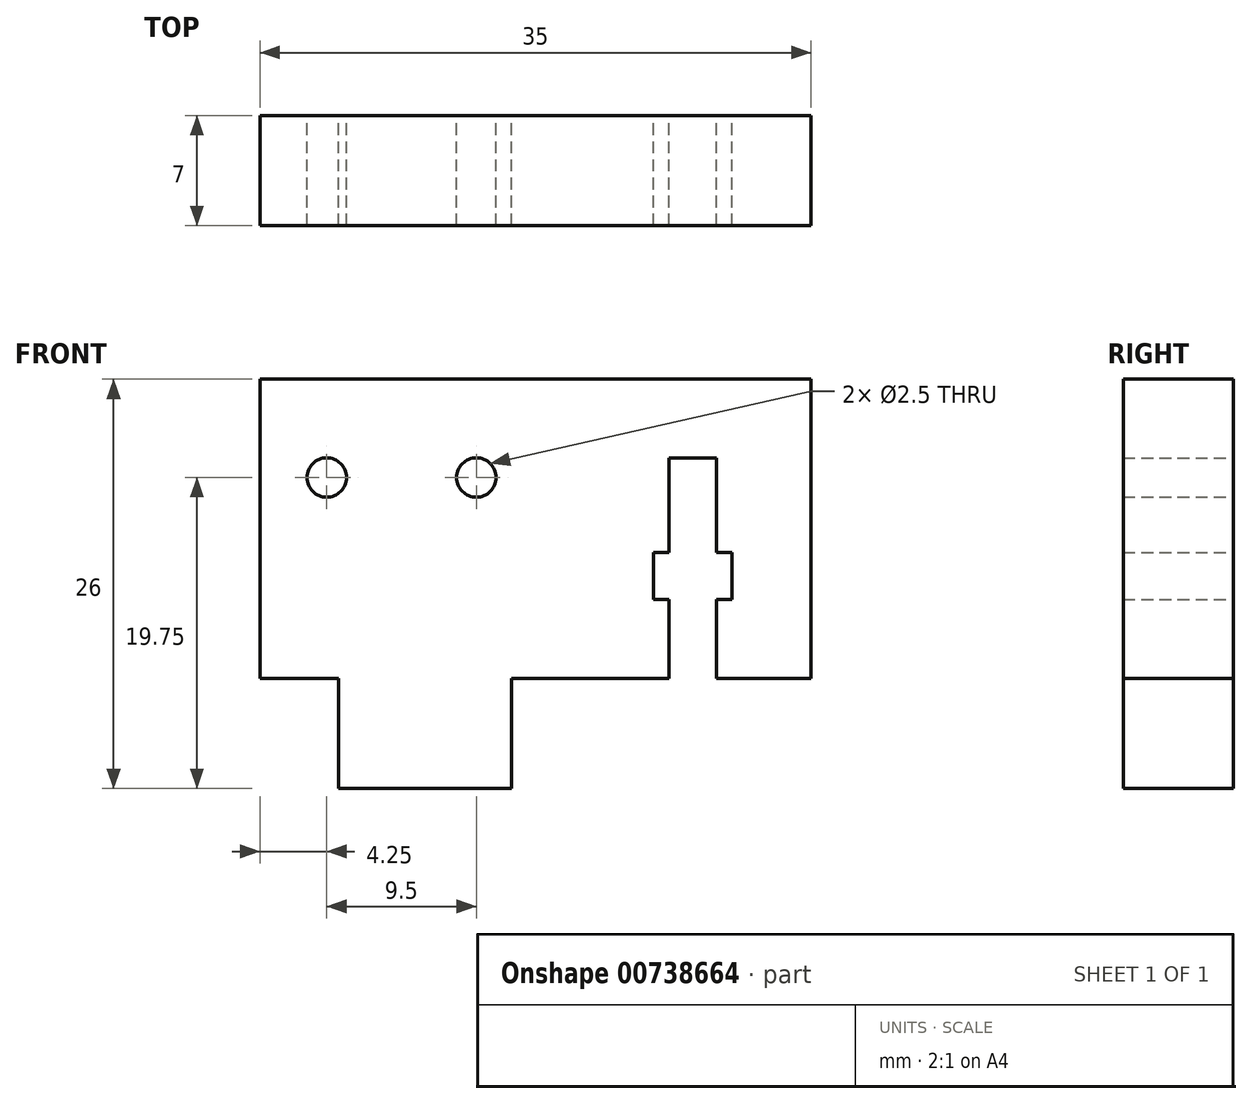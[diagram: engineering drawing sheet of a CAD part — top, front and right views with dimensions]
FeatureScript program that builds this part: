
annotation { "Feature Type Name" : "Feature", "Feature Type Description" : "" }
export const myFeature = defineFeature(function(context is Context, id is Id, definition is map)
    precondition{}
    {
        {
            var Q0;
            Q0=qCreatedBy(makeId("Front.planeOp"),FACE);
            var sketch = newSketch(context, id + "F0", { "sketchPlane" : qUnion([Q0])});
            skLineSegment(sketch, "E0", {"start": v(0, 0) * mm, "end": v(0, 26) * mm});
            skLineSegment(sketch, "E1", {"start": v(0, 26) * mm, "end": v(30, 26) * mm});
            skLineSegment(sketch, "E2", {"start": v(30, 26) * mm, "end": v(30, 7) * mm});
            skLineSegment(sketch, "E3", {"start": v(30, 7) * mm, "end": v(24, 7) * mm});
            skLineSegment(sketch, "E4", {"start": v(24, 7) * mm, "end": v(24, 12) * mm});
            skLineSegment(sketch, "E5", {"start": v(24, 12) * mm, "end": v(25, 12) * mm});
            skLineSegment(sketch, "E6", {"start": v(25, 12) * mm, "end": v(25, 15) * mm});
            skLineSegment(sketch, "E7", {"start": v(25, 15) * mm, "end": v(24, 15) * mm});
            skLineSegment(sketch, "E8", {"start": v(24, 15) * mm, "end": v(24, 21) * mm});
            skLineSegment(sketch, "E9", {"start": v(24, 21) * mm, "end": v(21, 21) * mm});
            skLineSegment(sketch, "E10", {"start": v(21, 21) * mm, "end": v(21, 15) * mm});
            skLineSegment(sketch, "E11", {"start": v(21, 15) * mm, "end": v(20, 15) * mm});
            skLineSegment(sketch, "E12", {"start": v(20, 15) * mm, "end": v(20, 12) * mm});
            skLineSegment(sketch, "E13", {"start": v(20, 12) * mm, "end": v(21, 12) * mm});
            skLineSegment(sketch, "E14", {"start": v(21, 12) * mm, "end": v(21, 7) * mm});
            skLineSegment(sketch, "E15", {"start": v(21, 7) * mm, "end": v(11, 7) * mm});
            skLineSegment(sketch, "E16", {"start": v(11, 7) * mm, "end": v(11, 0) * mm});
            skLineSegment(sketch, "E17", {"start": v(11, 0) * mm, "end": v(0, 0) * mm});
            skLineSegment(sketch, "E18.bottom", {"start": v(0, 26) * mm, "end": v(-5, 26) * mm});
            skLineSegment(sketch, "E18.top", {"start": v(0, 7) * mm, "end": v(-5, 7) * mm});
            skLineSegment(sketch, "E18.left", {"start": v(0, 26) * mm, "end": v(0, 7) * mm});
            skLineSegment(sketch, "E18.right", {"start": v(-5, 26) * mm, "end": v(-5, 7) * mm});
            skCircle(sketch, "E19", {"center": v(-0.75, 19.75) * mm, "radius": 1.25 * mm});
            skCircle(sketch, "E20", {"center": v(8.75, 19.75) * mm, "radius": 1.25 * mm});
            skSolve(sketch);
        }
        {
            var Q0;
            Q0 = qSketchRegion(id + "F0", true);
            extrude(context, id + "F1", {"entities" : qUnion([Q0]), "depth" : 7 * mm, "offsetDistance" : 25 * mm});
        }
    });
